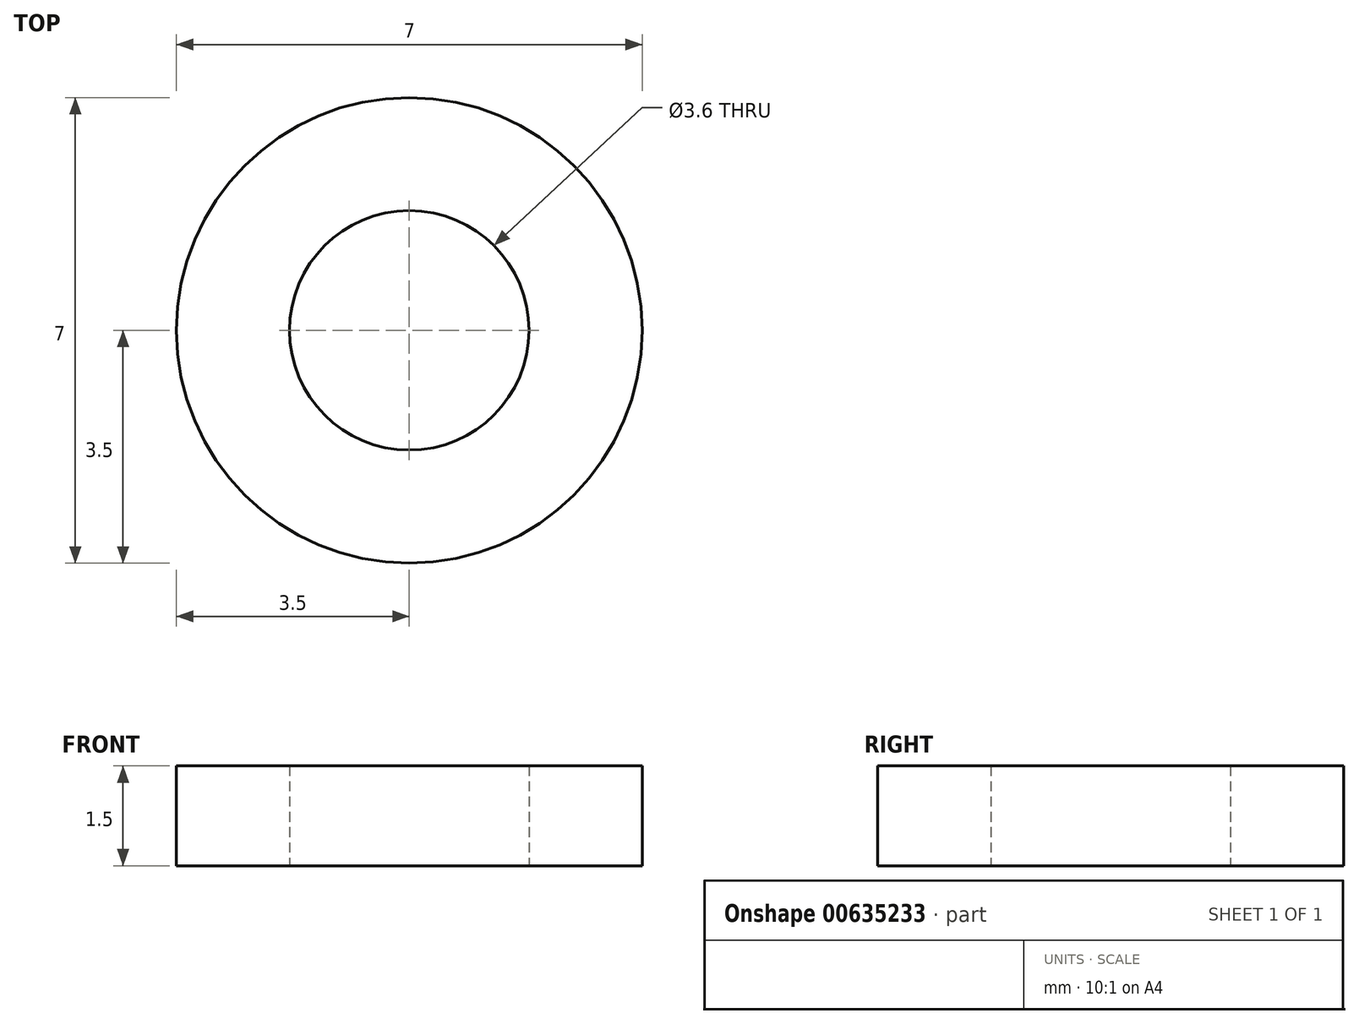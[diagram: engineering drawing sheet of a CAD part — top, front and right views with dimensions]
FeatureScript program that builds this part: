
annotation { "Feature Type Name" : "Feature", "Feature Type Description" : "" }
export const myFeature = defineFeature(function(context is Context, id is Id, definition is map)
    precondition{}
    {
        {
            var Q0;
            Q0=qCreatedBy(makeId("Top.planeOp"),FACE);
            var sketch = newSketch(context, id + "F0", { "sketchPlane" : qUnion([Q0])});
            skCircle(sketch, "E0", {"center": v(0, 0) * mm, "radius": 3.5 * mm});
            skCircle(sketch, "E1", {"center": v(0, 0) * mm, "radius": 1.8 * mm});
            skSolve(sketch);
        }
        {
            var Q0;
            Q0=makeQuery(id+"F0.imprint","IMPRINT",FACE,{"disambiguationData":[TD([[makeQuery(id+"F0.imprint","IMPRINT",EDGE,{"derivedFrom":sQuery(id+"F0.wireOp",EDGE,"E0")}),1.0]])]});
            extrude(context, id + "F1", {"entities" : qUnion([Q0]), "depth" : 1.5 * mm, "offsetDistance" : 25 * mm});
        }
    });
